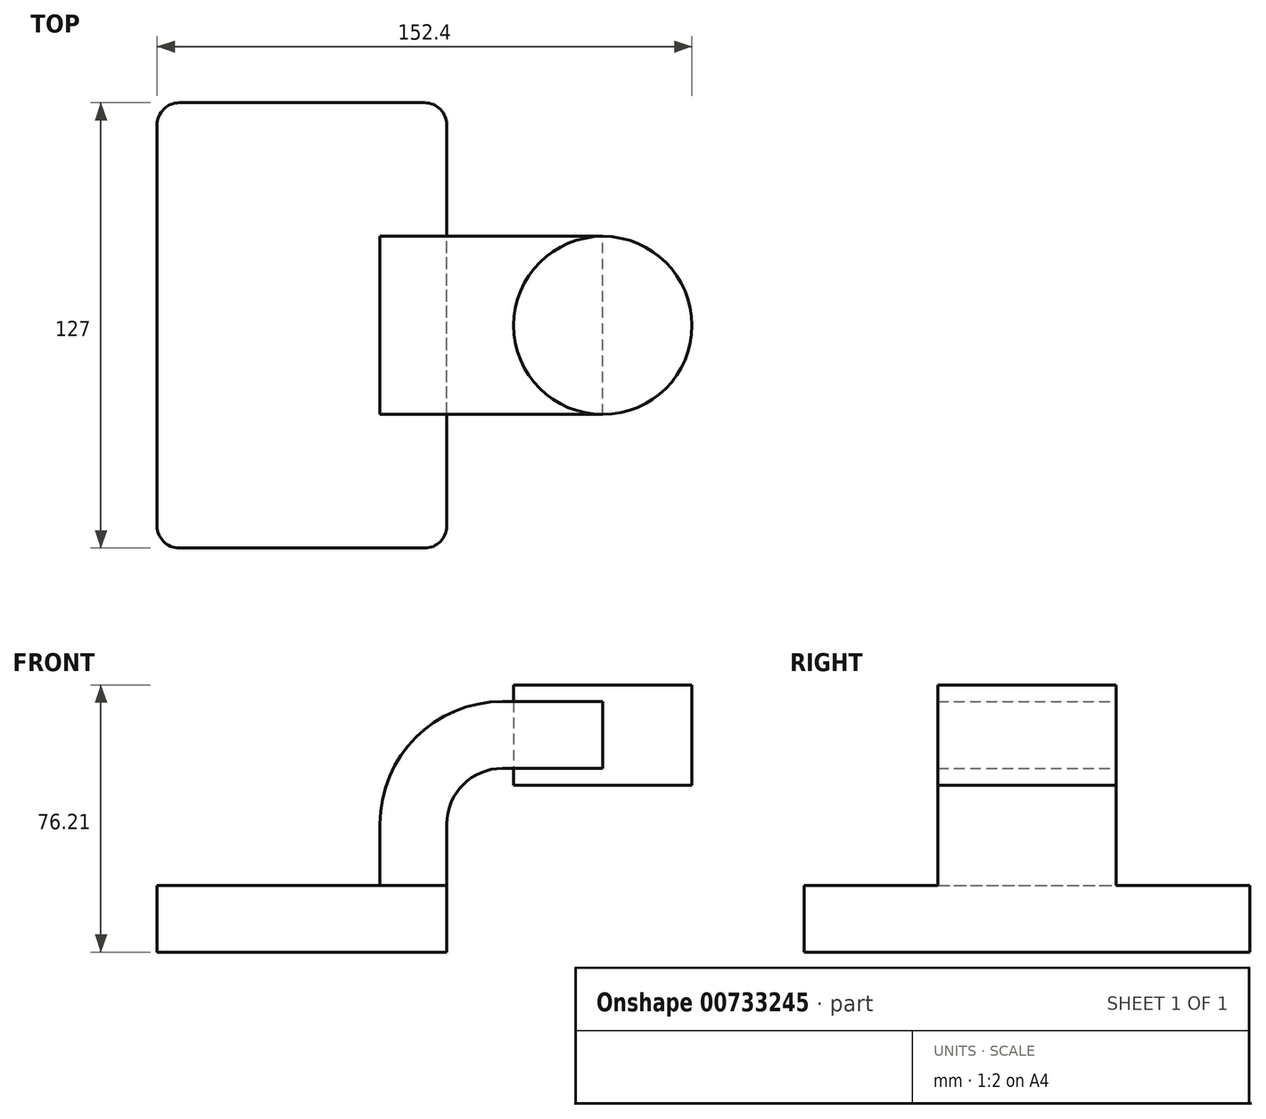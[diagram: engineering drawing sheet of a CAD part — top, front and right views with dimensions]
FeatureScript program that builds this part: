
annotation { "Feature Type Name" : "Feature", "Feature Type Description" : "" }
export const myFeature = defineFeature(function(context is Context, id is Id, definition is map)
    precondition{}
    {
        {
            var Q0;
            Q0=qCreatedBy(makeId("Front.planeOp"),FACE);
            var sketch = newSketch(context, id + "F0", { "sketchPlane" : qUnion([Q0])});
            skLineSegment(sketch, "E0.bottom", {"start": v(41.27, 9.53) * mm, "end": v(-41.28, 9.53) * mm});
            skLineSegment(sketch, "E0.top", {"start": v(41.28, -9.52) * mm, "end": v(-41.27, -9.52) * mm});
            skLineSegment(sketch, "E0.left", {"start": v(41.28, 9.53) * mm, "end": v(41.28, -9.52) * mm});
            skLineSegment(sketch, "E0.right", {"start": v(-41.28, 9.53) * mm, "end": v(-41.27, -9.52) * mm});
            skPoint(sketch, "E0.middle", {"position": v(0, 0) * mm});
            skLineSegment(sketch, "E1.bottom", {"start": v(111.12, 38.1) * mm, "end": v(60.32, 38.1) * mm});
            skLineSegment(sketch, "E1.top", {"start": v(111.13, 66.68) * mm, "end": v(60.33, 66.68) * mm});
            skLineSegment(sketch, "E1.left", {"start": v(111.12, 38.1) * mm, "end": v(111.13, 66.67) * mm});
            skLineSegment(sketch, "E1.right", {"start": v(60.32, 38.1) * mm, "end": v(60.33, 66.67) * mm});
            skPoint(sketch, "E1.middle", {"position": v(85.73, 52.39) * mm});
            skLineSegment(sketch, "E2", {"start": v(41.27, 9.53) * mm, "end": v(41.27, 27) * mm});
            skArc(sketch, "E3", {"start": v(41.27, 27) * mm, "mid": v(45.92, 38.23) * mm, "end": v(57.15, 42.88) * mm});
            skLineSegment(sketch, "E4", {"start": v(57.15, 42.88) * mm, "end": v(85.73, 42.88) * mm});
            skLineSegment(sketch, "E5.0", {"start": v(57.15, 61.93) * mm, "end": v(85.73, 61.93) * mm});
            skArc(sketch, "E5.1", {"start": v(22.23, 27) * mm, "mid": v(32.45, 51.7) * mm, "end": v(57.15, 61.93) * mm});
            skLineSegment(sketch, "E5.2", {"start": v(22.23, 9.53) * mm, "end": v(22.23, 27) * mm});
            skLineSegment(sketch, "E6", {"start": v(85.73, 38.1) * mm, "end": v(85.73, 66.68) * mm});
            skFitSpline(sketch, "E7", {"points": [v(-41.28, 9.53) * mm, v(57.15, 61.93) * mm], "startDerivative": vector(-3.16, 84.95) * mm, "endDerivative": vector(103.36, -10.72) * mm});
            skSolve(sketch);
        }
        {
            var Q0;
            Q0=makeQuery(id+"F0.imprint","IMPRINT",FACE,{"disambiguationData":[TD([[makeQuery(id+"F0.imprint","IMPRINT",EDGE,{"derivedFrom":sQuery(id+"F0.wireOp",EDGE,"E0.top")}),-1.0]])]});
            extrude(context, id + "F1", {"entities" : qUnion([Q0]), "endBound" : BoundingType.SYMMETRIC, "depth" : 127 * mm, "offsetDistance" : 25.4 * mm});
        }
        {
            var Q0;
            Q0=makeQuery(id+"F0.imprint","IMPRINT",FACE,{"disambiguationData":[TD([[makeQuery(id+"F0.imprint","IMPRINT",EDGE,{"derivedFrom":sQuery(id+"F0.wireOp",EDGE,"E5.1")}),1.0]])]});
            extrude(context, id + "F2", {"entities" : qUnion([Q0]), "operationType" : NewBodyOperationType.ADD, "endBound" : BoundingType.SYMMETRIC, "depth" : 15.88 * mm, "offsetDistance" : 25.4 * mm});
        }
        {
            var Q0;
            {var subQ1=sQuery(id+"F0.wireOp",EDGE,"E2");Q0=makeQuery(id+"F0.imprint","IMPRINT",FACE,{"disambiguationData":[TD([[makeQuery(id+"F0.imprint","IMPRINT",EDGE,{"derivedFrom":subQ1}),1.0]])]});}
            var Q1;
            {var subQ0=sQuery(id+"F0.wireOp",EDGE,"E4");var subQ1=sQuery(id+"F0.wireOp",EDGE,"E1.right");var subQ2=makeQuery(id+"F0.imprint","INTERSECT",VERTEX,{"derivedFrom":[subQ1,subQ0]});Q1=makeQuery(id+"F0.imprint","IMPRINT",FACE,{"disambiguationData":[TD([[makeQuery(id+"F0.imprint","IMPRINT",EDGE,{"disambiguationData":[TD([[subQ2,-1.0]])],"derivedFrom":subQ1}),-1.0]])]});}
            extrude(context, id + "F3", {"entities" : qUnion([Q0, Q1]), "operationType" : NewBodyOperationType.ADD, "endBound" : BoundingType.SYMMETRIC, "depth" : 50.8 * mm, "offsetDistance" : 25.4 * mm});
        }
        {
            var Q0;
            {var subQ4=sQuery(id+"F0.wireOp",EDGE,"E1.left");Q0=makeQuery(id+"F0.imprint","IMPRINT",FACE,{"disambiguationData":[TD([[makeQuery(id+"F0.imprint","IMPRINT",EDGE,{"derivedFrom":subQ4}),1.0]])]});}
            var Q1;
            Q1=sQuery(id+"F0.wireOp",EDGE,"E6");
            var Q2;
            Q2=sQuery(id+"F0.wireOp",EDGE,"E6");
            revolve(context, id + "F4", {"surfaceOperationType" : NewSurfaceOperationType.NEW, "entities" : qUnion([Q0]), "surfaceEntities" : qUnion([Q1]), "axis" : qUnion([Q2]), "revolveType" : RevolveType.FULL});
        }
        {
            var Q0;
            Q0=makeQuery(id+"F1.opExtrude","CAP_EDGE",EDGE,{"disambiguationData":[OSD([sQuery(id+"F0.wireOp",EDGE,"E0.right")])],"isStart":false});
            var Q1;
            Q1=makeQuery(id+"F1.opExtrude","CAP_EDGE",EDGE,{"disambiguationData":[OSD([sQuery(id+"F0.wireOp",EDGE,"E0.left")])],"isStart":false});
            var Q2;
            Q2=makeQuery(id+"F1.opExtrude","CAP_EDGE",EDGE,{"disambiguationData":[OSD([sQuery(id+"F0.wireOp",EDGE,"E0.left")])],"isStart":true});
            var Q3;
            Q3=makeQuery(id+"F1.opExtrude","CAP_EDGE",EDGE,{"disambiguationData":[OSD([sQuery(id+"F0.wireOp",EDGE,"E0.right")])],"isStart":true});
            fillet(context, id + "F5", {"entities" : qUnion([Q0, Q1, Q2, Q3]), "radius" : 6.35 * mm, "tangentPropagation" : true, "allowEdgeOverflow" : false});
        }
    });
